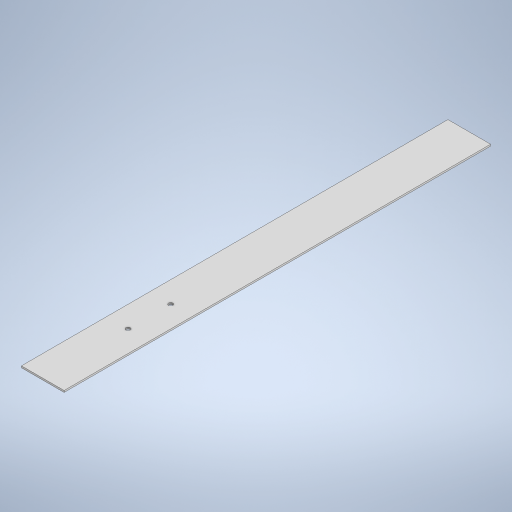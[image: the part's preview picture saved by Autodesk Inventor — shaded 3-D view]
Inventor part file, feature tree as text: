
AUTODESK INVENTOR PART (.ipt)
format: ipt  version: 2023 (Build 270158000, 158)  size: 236,032 bytes
history: native  units: mm
features: extrude x1, sketch x1
ambient origin geometry x8: Origin, YZ Plane, XZ Plane, XY Plane, X Axis, Y Axis, Z Axis, Center Point
bodies: Body1 (feature_tree)
feature tree (2):
  extrude  "Extrusion2"  Depth=500.0mm
  sketch  "Sketch1"  dims[d0=50.0mm d1=500.0mm d6=100.0mm d7=5.0mm d8=50.0mm d9=5.0mm d10=2.0mm d11=0.0mm]
